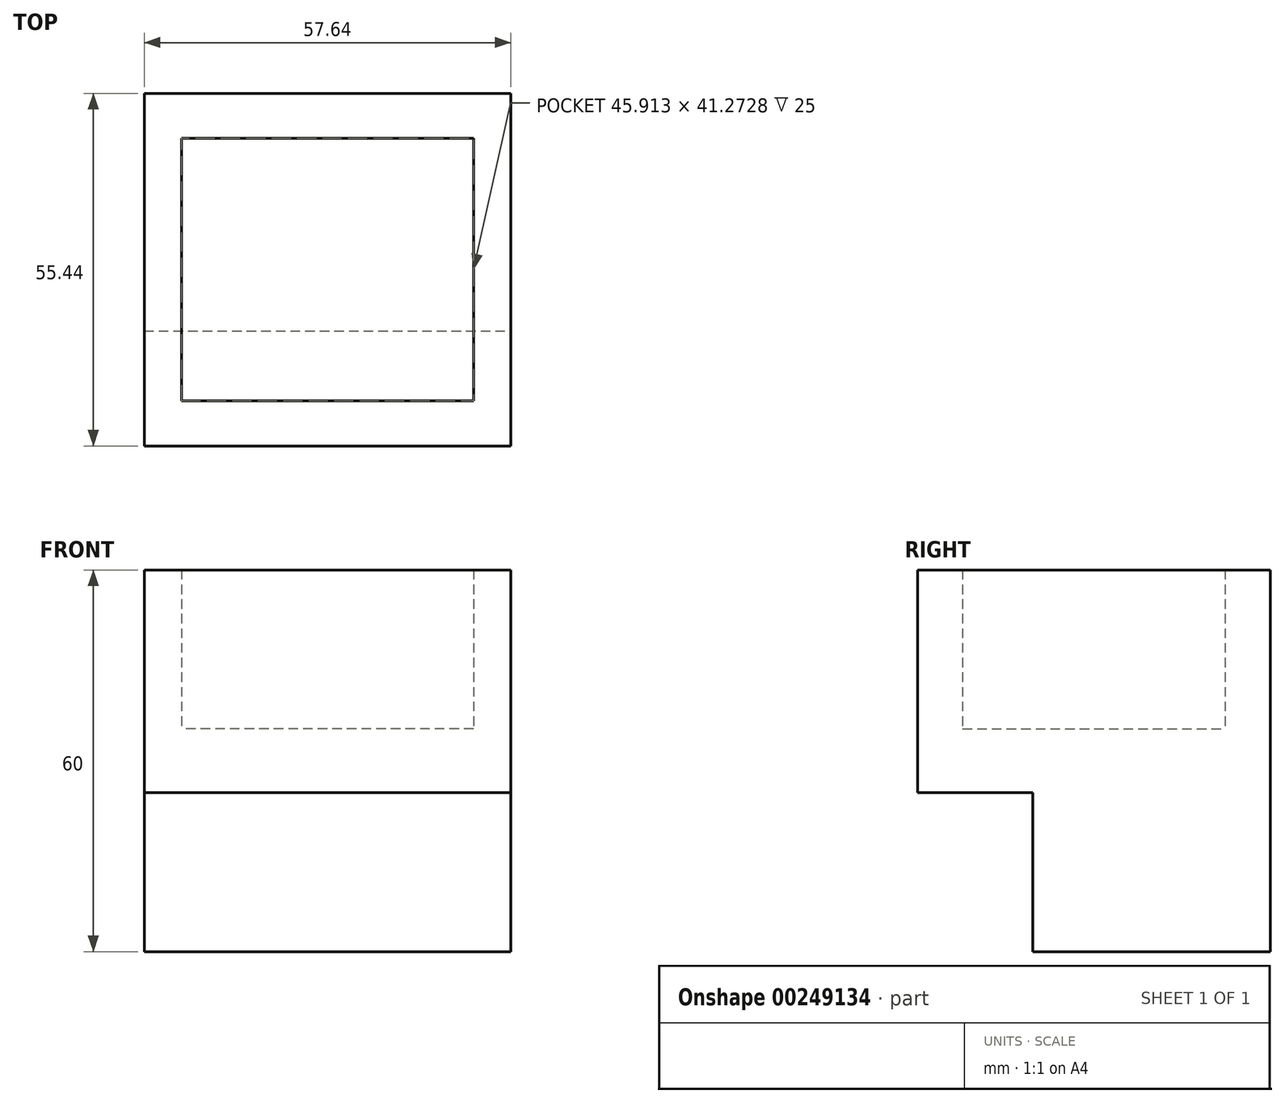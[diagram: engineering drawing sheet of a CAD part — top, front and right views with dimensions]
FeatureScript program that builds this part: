
annotation { "Feature Type Name" : "Feature", "Feature Type Description" : "" }
export const myFeature = defineFeature(function(context is Context, id is Id, definition is map)
    precondition{}
    {
        {
            var Q0;
            Q0=qCreatedBy(makeId("Top.planeOp"),FACE);
            var sketch = newSketch(context, id + "F0", { "sketchPlane" : qUnion([Q0])});
            skLineSegment(sketch, "E0.bottom", {"start": v(28.82, -27.72) * mm, "end": v(-28.82, -27.72) * mm});
            skLineSegment(sketch, "E0.top", {"start": v(28.82, 27.72) * mm, "end": v(-28.82, 27.72) * mm});
            skLineSegment(sketch, "E0.left", {"start": v(28.82, -27.72) * mm, "end": v(28.82, 27.72) * mm});
            skLineSegment(sketch, "E0.right", {"start": v(-28.82, -27.72) * mm, "end": v(-28.82, 27.72) * mm});
            skPoint(sketch, "E0.middle", {"position": v(0, 0) * mm});
            skLineSegment(sketch, "E1.bottom", {"start": v(22.96, -20.64) * mm, "end": v(-22.96, -20.64) * mm});
            skLineSegment(sketch, "E1.top", {"start": v(22.96, 20.64) * mm, "end": v(-22.96, 20.64) * mm});
            skLineSegment(sketch, "E1.left", {"start": v(22.96, -20.64) * mm, "end": v(22.96, 20.64) * mm});
            skLineSegment(sketch, "E1.right", {"start": v(-22.96, -20.64) * mm, "end": v(-22.96, 20.64) * mm});
            skSolve(sketch);
        }
        {
            var Q0;
            Q0 = qSketchRegion(id + "F0", true);
            extrude(context, id + "F1", {"entities" : qUnion([Q0]), "depth" : 25 * mm});
        }
        {
            var Q0;
            Q0=makeQuery(id+"F1.opExtrude","CAP_FACE",FACE,{"disambiguationData":[OSD([sQuery(id+"F0.wireOp",EDGE,"E0.bottom"),sQuery(id+"F0.wireOp",EDGE,"E0.top"),sQuery(id+"F0.wireOp",EDGE,"E0.left"),sQuery(id+"F0.wireOp",EDGE,"E0.right"),sQuery(id+"F0.wireOp",EDGE,"E1.bottom"),sQuery(id+"F0.wireOp",EDGE,"E1.top"),sQuery(id+"F0.wireOp",EDGE,"E1.left"),sQuery(id+"F0.wireOp",EDGE,"E1.right")])],"isStart":true});
            var sketch = newSketch(context, id + "F2", { "sketchPlane" : qUnion([Q0])});
            skLineSegment(sketch, "E2.bottom", {"start": v(28.82, -27.72) * mm, "end": v(-28.82, -27.72) * mm});
            skLineSegment(sketch, "E2.top", {"start": v(28.82, 27.72) * mm, "end": v(-28.82, 27.72) * mm});
            skLineSegment(sketch, "E2.left", {"start": v(28.82, -27.72) * mm, "end": v(28.82, 27.72) * mm});
            skLineSegment(sketch, "E2.right", {"start": v(-28.82, -27.72) * mm, "end": v(-28.82, 27.72) * mm});
            skPoint(sketch, "E2.middle", {"position": v(0, 0) * mm});
            skSolve(sketch);
        }
        {
            var Q0;
            Q0 = qSketchRegion(id + "F2", true);
            extrude(context, id + "F3", {"entities" : qUnion([Q0]), "operationType" : NewBodyOperationType.ADD, "depth" : 10 * mm});
        }
        {
            var Q0;
            Q0=makeQuery(id+"F3.opExtrude","CAP_FACE",FACE,{"disambiguationData":[OSD([sQuery(id+"F2.wireOp",EDGE,"E2.bottom"),sQuery(id+"F2.wireOp",EDGE,"E2.top"),sQuery(id+"F2.wireOp",EDGE,"E2.left"),sQuery(id+"F2.wireOp",EDGE,"E2.right")])],"isStart":false});
            var sketch = newSketch(context, id + "F4", { "sketchPlane" : qUnion([Q0])});
            skLineSegment(sketch, "E3.bottom", {"start": v(-28.82, -27.72) * mm, "end": v(28.82, -27.72) * mm});
            skLineSegment(sketch, "E3.top", {"start": v(-28.82, 9.65) * mm, "end": v(28.82, 9.65) * mm});
            skLineSegment(sketch, "E3.left", {"start": v(-28.82, -27.72) * mm, "end": v(-28.82, 9.65) * mm});
            skLineSegment(sketch, "E3.right", {"start": v(28.82, -27.72) * mm, "end": v(28.82, 9.65) * mm});
            skSolve(sketch);
        }
        {
            var Q0;
            Q0 = qSketchRegion(id + "F4", true);
            extrude(context, id + "F5", {"entities" : qUnion([Q0]), "operationType" : NewBodyOperationType.ADD, "depth" : 25 * mm});
        }
    });
